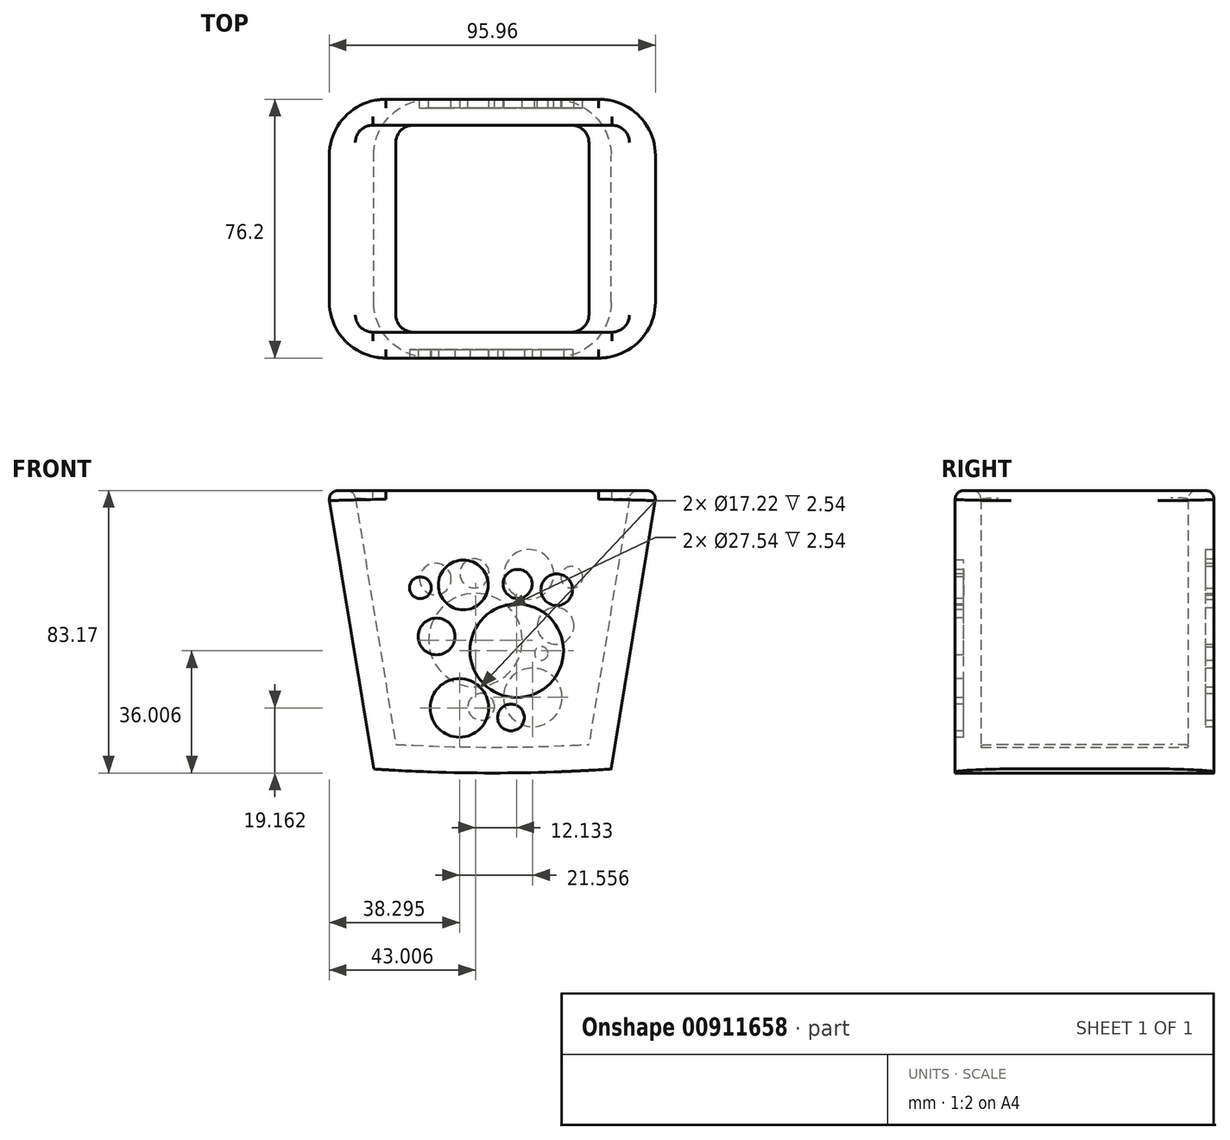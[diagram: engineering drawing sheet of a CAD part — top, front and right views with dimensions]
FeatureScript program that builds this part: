
annotation { "Feature Type Name" : "Feature", "Feature Type Description" : "" }
export const myFeature = defineFeature(function(context is Context, id is Id, definition is map)
    precondition{}
    {
        {
            var Q0;
            Q0=qCreatedBy(makeId("Front.planeOp"),FACE);
            var sketch = newSketch(context, id + "F0", { "sketchPlane" : qUnion([Q0])});
            skLineSegment(sketch, "E0", {"start": v(-48.43, 38.04) * mm, "end": v(-34.95, -43.94) * mm});
            skLineSegment(sketch, "E1.MirrorCS", {"start": v(48.43, 38.04) * mm, "end": v(34.95, -43.94) * mm});
            skArc(sketch, "E2", {"start": v(-34.95, -43.94) * mm, "mid": v(0, -45.13) * mm, "end": v(34.95, -43.94) * mm});
            skLineSegment(sketch, "E3", {"start": v(-48.43, 38.04) * mm, "end": v(48.43, 38.04) * mm});
            skSolve(sketch);
        }
        {
            var Q0;
            Q0=makeQuery(id+"F0.imprint","IMPRINT",FACE,{"disambiguationData":[TD([[makeQuery(id+"F0.imprint","IMPRINT",EDGE,{"derivedFrom":sQuery(id+"F0.wireOp",EDGE,"E0")}),1.0]])]});
            extrude(context, id + "F1", {"entities" : qUnion([Q0]), "endBound" : BoundingType.SYMMETRIC, "depth" : 76.2 * mm, "offsetDistance" : 25.4 * mm});
        }
        {
            var Q0;
            Q0=makeQuery(id+"F1.opExtrude","SWEPT_FACE",FACE,{"disambiguationData":[OSD([sQuery(id+"F0.wireOp",EDGE,"E3")])]});
            shell(context, id + "F2", {"entities" : qUnion([Q0]), "thickness" : 7.62 * mm});
        }
        {
            var Q0;
            Q0=makeQuery(id+"F1.opExtrude","CAP_EDGE",EDGE,{"disambiguationData":[OSD([sQuery(id+"F0.wireOp",EDGE,"E0")])],"isStart":false});
            var Q1;
            Q1=makeQuery(id+"F1.opExtrude","CAP_EDGE",EDGE,{"disambiguationData":[OSD([sQuery(id+"F0.wireOp",EDGE,"E1.MirrorCS")])],"isStart":false});
            var Q2;
            Q2=makeQuery(id+"F1.opExtrude","CAP_EDGE",EDGE,{"disambiguationData":[OSD([sQuery(id+"F0.wireOp",EDGE,"E1.MirrorCS")])],"isStart":true});
            var Q3;
            Q3=makeQuery(id+"F1.opExtrude","CAP_EDGE",EDGE,{"disambiguationData":[OSD([sQuery(id+"F0.wireOp",EDGE,"E0")])],"isStart":true});
            fillet(context, id + "F3", {"entities" : qUnion([Q0, Q1, Q2, Q3]), "radius" : 16.5 * mm, "tangentPropagation" : true, "allowEdgeOverflow" : false});
        }
        {
            var Q0;
            {var subQ0=sQuery(id+"F0.wireOp",EDGE,"E1.MirrorCS");Q0=makeQuery(id+"F2.opShell","OFFSET_EDGE",EDGE,{"disambiguationData":[OSD([subQ0]),TDD([makeQuery(id+"F1.opExtrude","CAP_EDGE",EDGE,{"disambiguationData":[OSD([subQ0])],"isStart":false})])]});}
            var Q1;
            {var subQ0=sQuery(id+"F0.wireOp",EDGE,"E0");Q1=makeQuery(id+"F2.opShell","OFFSET_EDGE",EDGE,{"disambiguationData":[OSD([subQ0]),TDD([makeQuery(id+"F1.opExtrude","CAP_EDGE",EDGE,{"disambiguationData":[OSD([subQ0])],"isStart":false})])]});}
            var Q2;
            {var subQ0=sQuery(id+"F0.wireOp",EDGE,"E0");Q2=makeQuery(id+"F2.opShell","OFFSET_EDGE",EDGE,{"disambiguationData":[OSD([subQ0]),TDD([makeQuery(id+"F1.opExtrude","CAP_EDGE",EDGE,{"disambiguationData":[OSD([subQ0])],"isStart":true})])]});}
            var Q3;
            {var subQ0=sQuery(id+"F0.wireOp",EDGE,"E1.MirrorCS");Q3=makeQuery(id+"F2.opShell","OFFSET_EDGE",EDGE,{"disambiguationData":[OSD([subQ0]),TDD([makeQuery(id+"F1.opExtrude","CAP_EDGE",EDGE,{"disambiguationData":[OSD([subQ0])],"isStart":true})])]});}
            fillet(context, id + "F4", {"entities" : qUnion([Q0, Q1, Q2, Q3]), "radius" : 5.08 * mm, "tangentPropagation" : true, "allowEdgeOverflow" : false});
        }
        {
            var Q0;
            Q0=makeQuery(id+"F1.opExtrude","CAP_FACE",FACE,{"disambiguationData":[OSD([sQuery(id+"F0.wireOp",EDGE,"E0"),sQuery(id+"F0.wireOp",EDGE,"E1.MirrorCS"),sQuery(id+"F0.wireOp",EDGE,"E2"),sQuery(id+"F0.wireOp",EDGE,"E3")])],"isStart":false});
            var sketch = newSketch(context, id + "F5", { "sketchPlane" : qUnion([Q0])});
            skCircle(sketch, "E4", {"center": v(-8.56, 10.25) * mm, "radius": 7.32 * mm});
            skCircle(sketch, "E5", {"center": v(7.16, -9.12) * mm, "radius": 13.77 * mm});
            skCircle(sketch, "E6", {"center": v(-16.42, -4.91) * mm, "radius": 5.4 * mm});
            skCircle(sketch, "E7", {"center": v(7.44, 10.53) * mm, "radius": 4.29 * mm});
            skCircle(sketch, "E8", {"center": v(-9.69, -25.97) * mm, "radius": 8.61 * mm});
            skCircle(sketch, "E9", {"center": v(5.47, -28.78) * mm, "radius": 3.93 * mm});
            skCircle(sketch, "E10", {"center": v(-12.21, -13.05) * mm, "radius": 1.99 * mm});
            skCircle(sketch, "E11", {"center": v(-21.2, 9.4) * mm, "radius": 3.2 * mm});
            skCircle(sketch, "E12", {"center": v(18.95, 8.84) * mm, "radius": 4.65 * mm});
            skSolve(sketch);
        }
        {
            var Q0;
            Q0=makeQuery(id+"F5.imprint","IMPRINT",FACE,{"disambiguationData":[TD([[makeQuery(id+"F5.imprint","IMPRINT",EDGE,{"derivedFrom":sQuery(id+"F5.wireOp",EDGE,"E6")}),1.0]])]});
            var Q1;
            Q1=makeQuery(id+"F5.imprint","IMPRINT",FACE,{"disambiguationData":[TD([[makeQuery(id+"F5.imprint","IMPRINT",EDGE,{"derivedFrom":sQuery(id+"F5.wireOp",EDGE,"E11")}),1.0]])]});
            var Q2;
            Q2=makeQuery(id+"F5.imprint","IMPRINT",FACE,{"disambiguationData":[TD([[makeQuery(id+"F5.imprint","IMPRINT",EDGE,{"derivedFrom":sQuery(id+"F5.wireOp",EDGE,"E4")}),1.0]])]});
            var Q3;
            Q3=makeQuery(id+"F5.imprint","IMPRINT",FACE,{"disambiguationData":[TD([[makeQuery(id+"F5.imprint","IMPRINT",EDGE,{"derivedFrom":sQuery(id+"F5.wireOp",EDGE,"E7")}),1.0]])]});
            var Q4;
            Q4=makeQuery(id+"F5.imprint","IMPRINT",FACE,{"disambiguationData":[TD([[makeQuery(id+"F5.imprint","IMPRINT",EDGE,{"derivedFrom":sQuery(id+"F5.wireOp",EDGE,"E12")}),1.0]])]});
            var Q5;
            Q5=makeQuery(id+"F5.imprint","IMPRINT",FACE,{"disambiguationData":[TD([[makeQuery(id+"F5.imprint","IMPRINT",EDGE,{"derivedFrom":sQuery(id+"F5.wireOp",EDGE,"E5")}),1.0]])]});
            var Q6;
            Q6=makeQuery(id+"F5.imprint","IMPRINT",FACE,{"disambiguationData":[TD([[makeQuery(id+"F5.imprint","IMPRINT",EDGE,{"derivedFrom":sQuery(id+"F5.wireOp",EDGE,"E8")}),1.0]])]});
            var Q7;
            Q7=makeQuery(id+"F5.imprint","IMPRINT",FACE,{"disambiguationData":[TD([[makeQuery(id+"F5.imprint","IMPRINT",EDGE,{"derivedFrom":sQuery(id+"F5.wireOp",EDGE,"E9")}),1.0]])]});
            extrude(context, id + "F6", {"entities" : qUnion([Q0, Q1, Q2, Q3, Q4, Q5, Q6, Q7]), "operationType" : NewBodyOperationType.REMOVE, "oppositeDirection" : true, "depth" : 2.54 * mm, "offsetDistance" : 25.4 * mm});
        }
        {
            var Q0;
            Q0=makeQuery(id+"F1.opExtrude","CAP_FACE",FACE,{"disambiguationData":[OSD([sQuery(id+"F0.wireOp",EDGE,"E0"),sQuery(id+"F0.wireOp",EDGE,"E1.MirrorCS"),sQuery(id+"F0.wireOp",EDGE,"E2"),sQuery(id+"F0.wireOp",EDGE,"E3")])],"isStart":true});
            var sketch = newSketch(context, id + "F7", { "sketchPlane" : qUnion([Q0])});
            skCircle(sketch, "E13", {"center": v(-10.75, 13.38) * mm, "radius": 7.32 * mm});
            skCircle(sketch, "E14", {"center": v(4.97, -6) * mm, "radius": 13.77 * mm});
            skCircle(sketch, "E15", {"center": v(-18.6, -1.78) * mm, "radius": 5.4 * mm});
            skCircle(sketch, "E16", {"center": v(5.25, 13.66) * mm, "radius": 4.29 * mm});
            skCircle(sketch, "E17", {"center": v(-11.87, -22.84) * mm, "radius": 8.61 * mm});
            skCircle(sketch, "E18", {"center": v(3.29, -25.64) * mm, "radius": 3.93 * mm});
            skCircle(sketch, "E19", {"center": v(-14.4, -9.92) * mm, "radius": 1.99 * mm});
            skCircle(sketch, "E20", {"center": v(-23.38, 12.54) * mm, "radius": 3.2 * mm});
            skCircle(sketch, "E21", {"center": v(16.76, 11.97) * mm, "radius": 4.65 * mm});
            skSolve(sketch);
        }
        {
            var Q0;
            Q0=makeQuery(id+"F7.imprint","IMPRINT",FACE,{"disambiguationData":[TD([[makeQuery(id+"F7.imprint","IMPRINT",EDGE,{"derivedFrom":sQuery(id+"F7.wireOp",EDGE,"E20")}),1.0]])]});
            var Q1;
            Q1=makeQuery(id+"F7.imprint","IMPRINT",FACE,{"disambiguationData":[TD([[makeQuery(id+"F7.imprint","IMPRINT",EDGE,{"derivedFrom":sQuery(id+"F7.wireOp",EDGE,"E13")}),1.0]])]});
            var Q2;
            Q2=makeQuery(id+"F7.imprint","IMPRINT",FACE,{"disambiguationData":[TD([[makeQuery(id+"F7.imprint","IMPRINT",EDGE,{"derivedFrom":sQuery(id+"F7.wireOp",EDGE,"E16")}),1.0]])]});
            var Q3;
            Q3=makeQuery(id+"F7.imprint","IMPRINT",FACE,{"disambiguationData":[TD([[makeQuery(id+"F7.imprint","IMPRINT",EDGE,{"derivedFrom":sQuery(id+"F7.wireOp",EDGE,"E21")}),1.0]])]});
            var Q4;
            Q4=makeQuery(id+"F7.imprint","IMPRINT",FACE,{"disambiguationData":[TD([[makeQuery(id+"F7.imprint","IMPRINT",EDGE,{"derivedFrom":sQuery(id+"F7.wireOp",EDGE,"E14")}),1.0]])]});
            var Q5;
            Q5=makeQuery(id+"F7.imprint","IMPRINT",FACE,{"disambiguationData":[TD([[makeQuery(id+"F7.imprint","IMPRINT",EDGE,{"derivedFrom":sQuery(id+"F7.wireOp",EDGE,"E15")}),1.0]])]});
            var Q6;
            Q6=makeQuery(id+"F7.imprint","IMPRINT",FACE,{"disambiguationData":[TD([[makeQuery(id+"F7.imprint","IMPRINT",EDGE,{"derivedFrom":sQuery(id+"F7.wireOp",EDGE,"E17")}),1.0]])]});
            var Q7;
            Q7=makeQuery(id+"F7.imprint","IMPRINT",FACE,{"disambiguationData":[TD([[makeQuery(id+"F7.imprint","IMPRINT",EDGE,{"derivedFrom":sQuery(id+"F7.wireOp",EDGE,"E18")}),1.0]])]});
            var Q8;
            Q8=makeQuery(id+"F7.imprint","IMPRINT",FACE,{"disambiguationData":[TD([[makeQuery(id+"F7.imprint","IMPRINT",EDGE,{"derivedFrom":sQuery(id+"F7.wireOp",EDGE,"E19")}),1.0]])]});
            extrude(context, id + "F8", {"entities" : qUnion([Q0, Q1, Q2, Q3, Q4, Q5, Q6, Q7, Q8]), "operationType" : NewBodyOperationType.REMOVE, "oppositeDirection" : true, "depth" : 2.54 * mm, "offsetDistance" : 25.4 * mm});
        }
        {
            var Q0;
            Q0=makeQuery(id+"F1.opExtrude","CAP_EDGE",EDGE,{"disambiguationData":[OSD([sQuery(id+"F0.wireOp",EDGE,"E3")])],"isStart":false});
            var Q1;
            Q1=makeQuery(id+"F1.opExtrude","SWEPT_EDGE",EDGE,{"disambiguationData":[OSD([sQuery(id+"F0.wireOp",EDGE,"E1.MirrorCS"),sQuery(id+"F0.wireOp",EDGE,"E3")])]});
            var Q2;
            Q2=makeQuery(id+"F1.opExtrude","CAP_EDGE",EDGE,{"disambiguationData":[OSD([sQuery(id+"F0.wireOp",EDGE,"E3")])],"isStart":true});
            var Q3;
            Q3=makeQuery(id+"F1.opExtrude","SWEPT_EDGE",EDGE,{"disambiguationData":[OSD([sQuery(id+"F0.wireOp",EDGE,"E0"),sQuery(id+"F0.wireOp",EDGE,"E3")])]});
            var Q4;
            Q4=makeQuery(id+"F2.opShell","OFFSET_EDGE",EDGE,{"disambiguationData":[OSD([sQuery(id+"F0.wireOp",EDGE,"E0"),sQuery(id+"F0.wireOp",EDGE,"E3")])]});
            fillet(context, id + "F9", {"entities" : qUnion([Q0, Q1, Q2, Q3, Q4]), "radius" : 2.54 * mm, "tangentPropagation" : true, "allowEdgeOverflow" : false});
        }
    });
